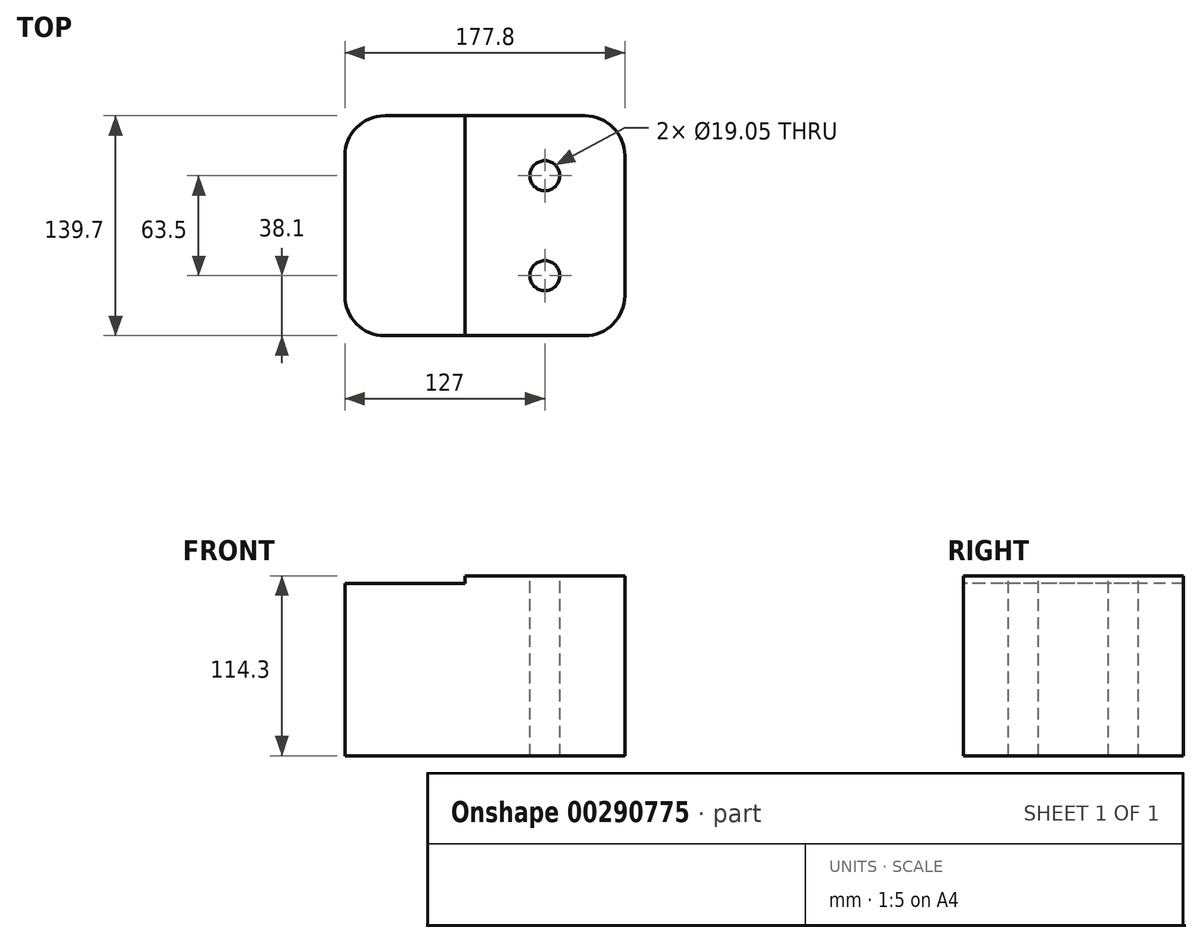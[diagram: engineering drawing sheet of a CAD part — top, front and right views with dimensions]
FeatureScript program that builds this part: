
annotation { "Feature Type Name" : "Feature", "Feature Type Description" : "" }
export const myFeature = defineFeature(function(context is Context, id is Id, definition is map)
    precondition{}
    {
        {
            var Q0;
            Q0=qCreatedBy(makeId("Top.planeOp"),FACE);
            var sketch = newSketch(context, id + "F0", { "sketchPlane" : qUnion([Q0])});
            skLineSegment(sketch, "E0.bottom", {"start": v(0, 139.7) * mm, "end": v(177.8, 139.7) * mm});
            skLineSegment(sketch, "E0.top", {"start": v(0, 0) * mm, "end": v(177.8, 0) * mm});
            skLineSegment(sketch, "E0.left", {"start": v(0, 139.7) * mm, "end": v(0, 0) * mm});
            skLineSegment(sketch, "E0.right", {"start": v(177.8, 139.7) * mm, "end": v(177.8, 0) * mm});
            skSolve(sketch);
        }
        {
            var Q0;
            Q0 = qSketchRegion(id + "F0", true);
            extrude(context, id + "F1", {"entities" : qUnion([Q0]), "depth" : 114.3 * mm});
        }
        {
            var Q0;
            Q0=makeQuery(id+"F1.opExtrude","CAP_FACE",FACE,{"disambiguationData":[OSD([sQuery(id+"F0.wireOp",EDGE,"E0.bottom"),sQuery(id+"F0.wireOp",EDGE,"E0.top"),sQuery(id+"F0.wireOp",EDGE,"E0.left"),sQuery(id+"F0.wireOp",EDGE,"E0.right")])],"isStart":false});
            var sketch = newSketch(context, id + "F2", { "sketchPlane" : qUnion([Q0])});
            skLineSegment(sketch, "E1.bottom", {"start": v(0, 139.7) * mm, "end": v(76.2, 139.7) * mm});
            skLineSegment(sketch, "E1.top", {"start": v(0, 0) * mm, "end": v(76.2, 0) * mm});
            skLineSegment(sketch, "E1.left", {"start": v(0, 139.7) * mm, "end": v(0, 0) * mm});
            skLineSegment(sketch, "E1.right", {"start": v(76.2, 139.7) * mm, "end": v(76.2, 0) * mm});
            skSolve(sketch);
        }
        {
            var Q0;
            Q0 = qSketchRegion(id + "F2", true);
            extrude(context, id + "F3", {"entities" : qUnion([Q0]), "operationType" : NewBodyOperationType.REMOVE, "oppositeDirection" : true, "depth" : 4.76 * mm});
        }
        {
            var Q0;
            Q0=makeQuery(id+"F1.opExtrude","CAP_FACE",FACE,{"disambiguationData":[OSD([sQuery(id+"F0.wireOp",EDGE,"E0.bottom"),sQuery(id+"F0.wireOp",EDGE,"E0.top"),sQuery(id+"F0.wireOp",EDGE,"E0.left"),sQuery(id+"F0.wireOp",EDGE,"E0.right")])],"isStart":false});
            var sketch = newSketch(context, id + "F4", { "sketchPlane" : qUnion([Q0])});
            skCircle(sketch, "E2", {"center": v(127, 101.6) * mm, "radius": 9.53 * mm});
            skCircle(sketch, "E3", {"center": v(127, 38.1) * mm, "radius": 9.53 * mm});
            skSolve(sketch);
        }
        {
            var Q0;
            Q0 = qSketchRegion(id + "F4", true);
            extrude(context, id + "F5", {"entities" : qUnion([Q0]), "operationType" : NewBodyOperationType.REMOVE, "endBound" : BoundingType.THROUGH_ALL, "oppositeDirection" : true, "depth" : 25.4 * mm});
        }
        {
            var Q0;
            Q0=makeQuery(id+"F1.opExtrude","SWEPT_EDGE",EDGE,{"disambiguationData":[OSD([sQuery(id+"F0.wireOp",EDGE,"E0.top"),sQuery(id+"F0.wireOp",EDGE,"E0.left")])]});
            var Q1;
            Q1=makeQuery(id+"F1.opExtrude","SWEPT_EDGE",EDGE,{"disambiguationData":[OSD([sQuery(id+"F0.wireOp",EDGE,"E0.top"),sQuery(id+"F0.wireOp",EDGE,"E0.right")])]});
            var Q2;
            Q2=makeQuery(id+"F1.opExtrude","SWEPT_EDGE",EDGE,{"disambiguationData":[OSD([sQuery(id+"F0.wireOp",EDGE,"E0.bottom"),sQuery(id+"F0.wireOp",EDGE,"E0.right")])]});
            var Q3;
            Q3=makeQuery(id+"F1.opExtrude","SWEPT_EDGE",EDGE,{"disambiguationData":[OSD([sQuery(id+"F0.wireOp",EDGE,"E0.bottom"),sQuery(id+"F0.wireOp",EDGE,"E0.left")])]});
            fillet(context, id + "F6", {"entities" : qUnion([Q0, Q1, Q2, Q3]), "radius" : 25.4 * mm, "tangentPropagation" : true, "allowEdgeOverflow" : false});
        }
    });
